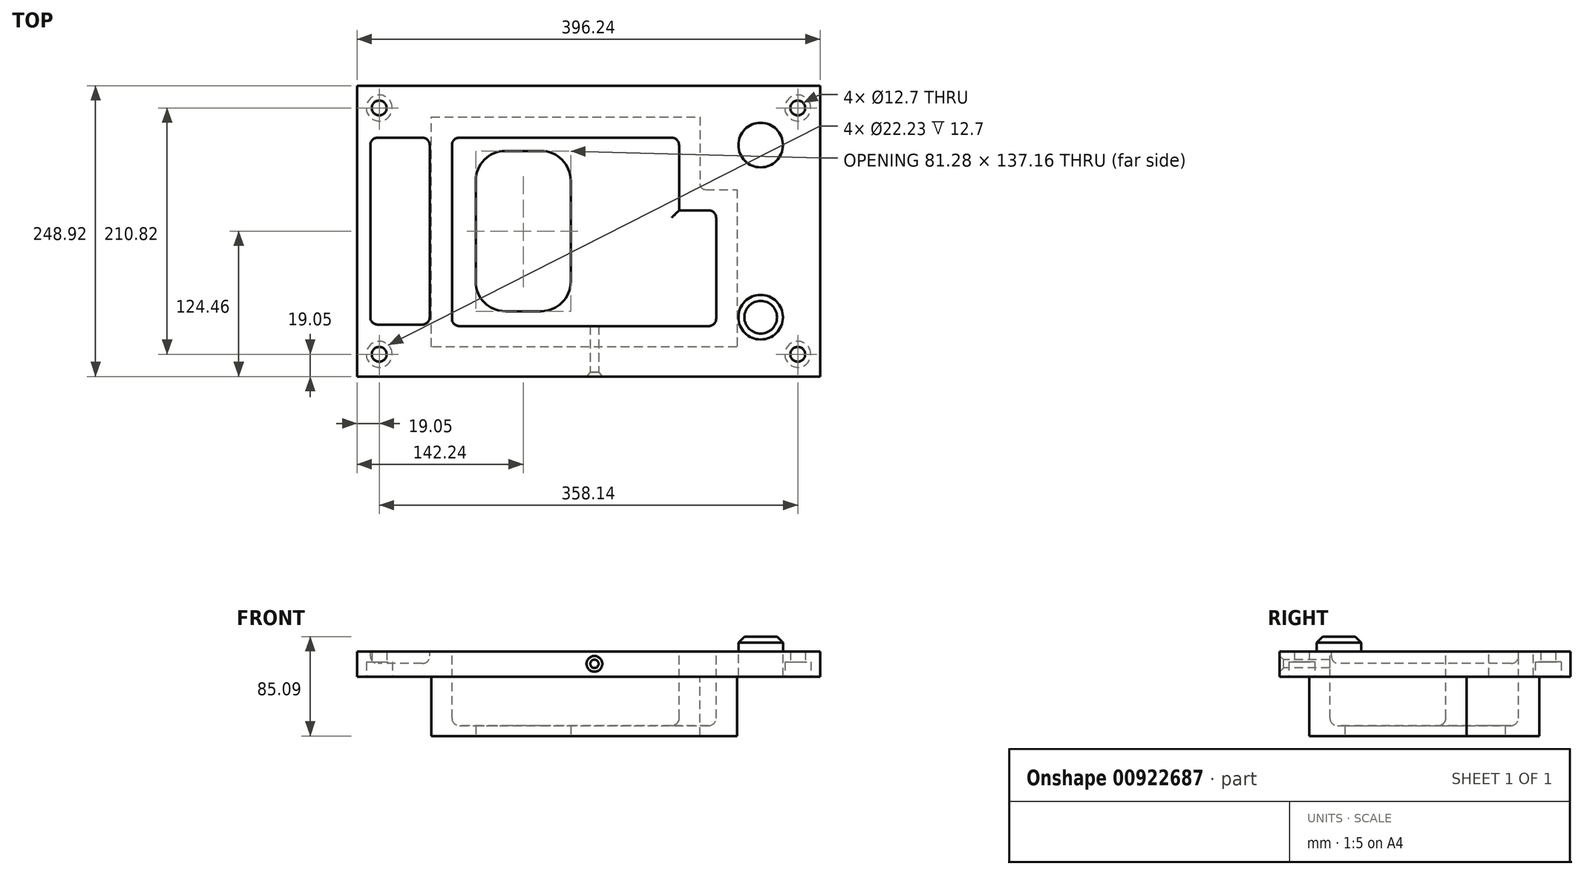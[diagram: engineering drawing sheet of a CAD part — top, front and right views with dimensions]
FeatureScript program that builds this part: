
annotation { "Feature Type Name" : "Feature", "Feature Type Description" : "" }
export const myFeature = defineFeature(function(context is Context, id is Id, definition is map)
    precondition{}
    {
        {
            var Q0;
            Q0=qCreatedBy(makeId("Top.planeOp"),FACE);
            var sketch = newSketch(context, id + "F0", { "sketchPlane" : qUnion([Q0])});
            skLineSegment(sketch, "E0.bottom", {"start": v(198.12, 124.46) * mm, "end": v(-198.12, 124.46) * mm});
            skLineSegment(sketch, "E0.top", {"start": v(198.12, -124.46) * mm, "end": v(-198.12, -124.46) * mm});
            skLineSegment(sketch, "E0.left", {"start": v(198.12, 124.46) * mm, "end": v(198.12, -124.46) * mm});
            skLineSegment(sketch, "E0.right", {"start": v(-198.12, 124.46) * mm, "end": v(-198.12, -124.46) * mm});
            skPoint(sketch, "E0.middle", {"position": v(0, 0) * mm});
            skSolve(sketch);
        }
        {
            var Q0;
            Q0 = qSketchRegion(id + "F0", true);
            extrude(context, id + "F1", {"entities" : qUnion([Q0]), "oppositeDirection" : true, "depth" : 21.59 * mm, "offsetDistance" : 25.4 * mm});
        }
        {
            var Q0;
            Q0=makeQuery(id+"F1.opExtrude","CAP_FACE",FACE,{"disambiguationData":[OSD([sQuery(id+"F0.wireOp",EDGE,"E0.bottom"),sQuery(id+"F0.wireOp",EDGE,"E0.top"),sQuery(id+"F0.wireOp",EDGE,"E0.left"),sQuery(id+"F0.wireOp",EDGE,"E0.right")])],"isStart":false});
            var sketch = newSketch(context, id + "F2", { "sketchPlane" : qUnion([Q0])});
            skLineSegment(sketch, "E1", {"start": v(-134.62, 99.06) * mm, "end": v(-134.62, -97.79) * mm});
            skLineSegment(sketch, "E2", {"start": v(-134.62, -97.79) * mm, "end": v(95.25, -97.79) * mm});
            skLineSegment(sketch, "E3", {"start": v(95.25, -97.8) * mm, "end": v(95.25, -35.56) * mm});
            skLineSegment(sketch, "E4", {"start": v(95.25, -35.56) * mm, "end": v(127, -35.56) * mm});
            skLineSegment(sketch, "E5", {"start": v(127, -35.56) * mm, "end": v(127, 99.06) * mm});
            skLineSegment(sketch, "E6", {"start": v(127, 99.06) * mm, "end": v(-134.62, 99.06) * mm});
            skSolve(sketch);
        }
        {
            var Q0;
            Q0 = qSketchRegion(id + "F2", true);
            extrude(context, id + "F3", {"entities" : qUnion([Q0]), "operationType" : NewBodyOperationType.ADD, "depth" : 50.8 * mm, "offsetDistance" : 25.4 * mm});
        }
        {
            var Q0;
            Q0=makeQuery(id+"F1.opExtrude","CAP_FACE",FACE,{"disambiguationData":[OSD([sQuery(id+"F0.wireOp",EDGE,"E0.bottom"),sQuery(id+"F0.wireOp",EDGE,"E0.top"),sQuery(id+"F0.wireOp",EDGE,"E0.left"),sQuery(id+"F0.wireOp",EDGE,"E0.right")])],"isStart":true});
            var sketch = newSketch(context, id + "F4", { "sketchPlane" : qUnion([Q0])});
            skLineSegment(sketch, "E7.0", {"start": v(127, -99.06) * mm, "end": v(-134.62, -99.06) * mm, "construction": true});
            skLineSegment(sketch, "E8.0", {"start": v(127, 35.56) * mm, "end": v(127, -99.06) * mm, "construction": true});
            skPoint(sketch, "E9.0", {"position": v(111.12, 35.56) * mm});
            skLineSegment(sketch, "E10.0", {"start": v(95.25, 97.8) * mm, "end": v(95.25, 35.56) * mm, "construction": true});
            skLineSegment(sketch, "E11.0", {"start": v(95.25, 35.56) * mm, "end": v(127, 35.56) * mm, "construction": true});
            skLineSegment(sketch, "E12.0", {"start": v(-134.62, 97.79) * mm, "end": v(95.25, 97.79) * mm, "construction": true});
            skLineSegment(sketch, "E13.0", {"start": v(-134.62, -99.06) * mm, "end": v(-134.62, 97.79) * mm, "construction": true});
            skLineSegment(sketch, "E14", {"start": v(109.22, -81.28) * mm, "end": v(109.22, 17.78) * mm});
            skLineSegment(sketch, "E15", {"start": v(109.22, 17.78) * mm, "end": v(77.47, 17.78) * mm});
            skLineSegment(sketch, "E16", {"start": v(77.47, 17.78) * mm, "end": v(77.47, 80) * mm});
            skLineSegment(sketch, "E17", {"start": v(77.47, 80) * mm, "end": v(-116.84, 80) * mm});
            skLineSegment(sketch, "E18", {"start": v(-116.84, 80) * mm, "end": v(-116.84, -81.28) * mm});
            skLineSegment(sketch, "E19", {"start": v(-116.84, -81.28) * mm, "end": v(109.22, -81.28) * mm});
            skSolve(sketch);
        }
        {
            var Q0;
            Q0 = qSketchRegion(id + "F4", true);
            extrude(context, id + "F5", {"entities" : qUnion([Q0]), "operationType" : NewBodyOperationType.REMOVE, "oppositeDirection" : true, "depth" : 63.5 * mm, "offsetDistance" : 25.4 * mm});
        }
        {
            var Q0;
            Q0=makeQuery(id+"F5.boolean.opBoolean","COPY",FACE,{"derivedFrom":makeQuery(id+"F5.opExtrude","CAP_FACE",FACE,{"disambiguationData":[OSD([sQuery(id+"F4.wireOp",EDGE,"E14"),sQuery(id+"F4.wireOp",EDGE,"E15"),sQuery(id+"F4.wireOp",EDGE,"E16"),sQuery(id+"F4.wireOp",EDGE,"E17"),sQuery(id+"F4.wireOp",EDGE,"E18"),sQuery(id+"F4.wireOp",EDGE,"E19")])],"isStart":false})});
            var Q1;
            Q1=makeQuery(id+"F5.boolean.opBoolean","COPY",EDGE,{"derivedFrom":makeQuery(id+"F5.opExtrude","SWEPT_EDGE",EDGE,{"disambiguationData":[OSD([sQuery(id+"F4.wireOp",EDGE,"E14"),sQuery(id+"F4.wireOp",EDGE,"E19")])]})});
            var Q2;
            Q2=makeQuery(id+"F5.boolean.opBoolean","COPY",EDGE,{"derivedFrom":makeQuery(id+"F5.opExtrude","SWEPT_EDGE",EDGE,{"disambiguationData":[OSD([sQuery(id+"F4.wireOp",EDGE,"E18"),sQuery(id+"F4.wireOp",EDGE,"E19")])]})});
            var Q3;
            Q3=makeQuery(id+"F5.boolean.opBoolean","COPY",EDGE,{"derivedFrom":makeQuery(id+"F5.opExtrude","SWEPT_EDGE",EDGE,{"disambiguationData":[OSD([sQuery(id+"F4.wireOp",EDGE,"E17"),sQuery(id+"F4.wireOp",EDGE,"E18")])]})});
            var Q4;
            Q4=makeQuery(id+"F5.boolean.opBoolean","COPY",EDGE,{"derivedFrom":makeQuery(id+"F5.opExtrude","SWEPT_EDGE",EDGE,{"disambiguationData":[OSD([sQuery(id+"F4.wireOp",EDGE,"E14"),sQuery(id+"F4.wireOp",EDGE,"E15")])]})});
            var Q5;
            Q5=makeQuery(id+"F5.boolean.opBoolean","COPY",EDGE,{"derivedFrom":makeQuery(id+"F5.opExtrude","SWEPT_EDGE",EDGE,{"disambiguationData":[OSD([sQuery(id+"F4.wireOp",EDGE,"E16"),sQuery(id+"F4.wireOp",EDGE,"E17")])]})});
            fillet(context, id + "F6", {"entities" : qUnion([Q0, Q1, Q2, Q3, Q4, Q5]), "radius" : 6.35 * mm, "tangentPropagation" : true, "allowEdgeOverflow" : false});
        }
        {
            var Q0;
            Q0=makeQuery(id+"F3.opExtrude","SWEPT_EDGE",EDGE,{"disambiguationData":[OSD([sQuery(id+"F2.wireOp",EDGE,"E3"),sQuery(id+"F2.wireOp",EDGE,"E4")])]});
            fillet(context, id + "F7", {"entities" : qUnion([Q0]), "radius" : 5.08 * mm, "tangentPropagation" : true, "allowEdgeOverflow" : false});
        }
        {
            var Q0;
            Q0=makeQuery(id+"F3.opExtrude","CAP_FACE",FACE,{"disambiguationData":[OSD([sQuery(id+"F2.wireOp",EDGE,"E1"),sQuery(id+"F2.wireOp",EDGE,"E2"),sQuery(id+"F2.wireOp",EDGE,"E3"),sQuery(id+"F2.wireOp",EDGE,"E4"),sQuery(id+"F2.wireOp",EDGE,"E5"),sQuery(id+"F2.wireOp",EDGE,"E6")])],"isStart":false});
            var sketch = newSketch(context, id + "F8", { "sketchPlane" : qUnion([Q0])});
            skLineSegment(sketch, "E20.bottom", {"start": v(-96.52, -68.58) * mm, "end": v(-15.24, -68.58) * mm});
            skLineSegment(sketch, "E20.top", {"start": v(-96.52, 68.58) * mm, "end": v(-15.24, 68.58) * mm});
            skLineSegment(sketch, "E20.left", {"start": v(-96.52, -68.58) * mm, "end": v(-96.52, 68.58) * mm});
            skLineSegment(sketch, "E20.right", {"start": v(-15.24, -68.58) * mm, "end": v(-15.24, 68.58) * mm});
            skPoint(sketch, "E20.middle", {"position": v(-55.88, 0) * mm});
            skSolve(sketch);
        }
        {
            var Q0;
            Q0 = qSketchRegion(id + "F8", true);
            extrude(context, id + "F9", {"entities" : qUnion([Q0]), "operationType" : NewBodyOperationType.REMOVE, "endBound" : BoundingType.THROUGH_ALL, "oppositeDirection" : true, "depth" : 25.4 * mm, "offsetDistance" : 25.4 * mm});
        }
        {
            var Q0;
            Q0=makeQuery(id+"F1.opExtrude","CAP_FACE",FACE,{"disambiguationData":[OSD([sQuery(id+"F0.wireOp",EDGE,"E0.bottom"),sQuery(id+"F0.wireOp",EDGE,"E0.top"),sQuery(id+"F0.wireOp",EDGE,"E0.left"),sQuery(id+"F0.wireOp",EDGE,"E0.right")])],"isStart":true});
            var sketch = newSketch(context, id + "F10", { "sketchPlane" : qUnion([Q0])});
            skLineSegment(sketch, "E21.bottom", {"start": v(-135.9, 80) * mm, "end": v(-186.7, 80) * mm});
            skLineSegment(sketch, "E21.top", {"start": v(-135.9, -80) * mm, "end": v(-186.7, -80) * mm});
            skLineSegment(sketch, "E21.left", {"start": v(-135.9, 80) * mm, "end": v(-135.9, -80) * mm});
            skLineSegment(sketch, "E21.right", {"start": v(-186.7, 80) * mm, "end": v(-186.7, -80) * mm});
            skPoint(sketch, "E21.middle", {"position": v(-161.3, 0) * mm});
            skSolve(sketch);
        }
        {
            var Q0;
            Q0 = qSketchRegion(id + "F10", true);
            extrude(context, id + "F11", {"entities" : qUnion([Q0]), "operationType" : NewBodyOperationType.REMOVE, "oppositeDirection" : true, "depth" : 10.4 * mm, "offsetDistance" : 25.4 * mm});
        }
        {
            var Q0;
            Q0=makeQuery(id+"F11.boolean.opBoolean","COPY",FACE,{"derivedFrom":makeQuery(id+"F11.opExtrude","CAP_FACE",FACE,{"disambiguationData":[OSD([sQuery(id+"F10.wireOp",EDGE,"E21.bottom"),sQuery(id+"F10.wireOp",EDGE,"E21.top"),sQuery(id+"F10.wireOp",EDGE,"E21.left"),sQuery(id+"F10.wireOp",EDGE,"E21.right")])],"isStart":false})});
            var Q1;
            Q1=makeQuery(id+"F11.boolean.opBoolean","COPY",EDGE,{"derivedFrom":makeQuery(id+"F11.opExtrude","SWEPT_EDGE",EDGE,{"disambiguationData":[OSD([sQuery(id+"F10.wireOp",EDGE,"E21.bottom"),sQuery(id+"F10.wireOp",EDGE,"E21.right")])]})});
            var Q2;
            Q2=makeQuery(id+"F11.boolean.opBoolean","COPY",EDGE,{"derivedFrom":makeQuery(id+"F11.opExtrude","SWEPT_EDGE",EDGE,{"disambiguationData":[OSD([sQuery(id+"F10.wireOp",EDGE,"E21.bottom"),sQuery(id+"F10.wireOp",EDGE,"E21.left")])]})});
            var Q3;
            Q3=makeQuery(id+"F11.boolean.opBoolean","COPY",EDGE,{"derivedFrom":makeQuery(id+"F11.opExtrude","SWEPT_EDGE",EDGE,{"disambiguationData":[OSD([sQuery(id+"F10.wireOp",EDGE,"E21.top"),sQuery(id+"F10.wireOp",EDGE,"E21.left")])]})});
            var Q4;
            Q4=makeQuery(id+"F11.boolean.opBoolean","COPY",EDGE,{"derivedFrom":makeQuery(id+"F11.opExtrude","SWEPT_EDGE",EDGE,{"disambiguationData":[OSD([sQuery(id+"F10.wireOp",EDGE,"E21.top"),sQuery(id+"F10.wireOp",EDGE,"E21.right")])]})});
            fillet(context, id + "F12", {"entities" : qUnion([Q0, Q1, Q2, Q3, Q4]), "radius" : 6.35 * mm, "tangentPropagation" : true, "allowEdgeOverflow" : false});
        }
        {
            var Q0;
            Q0=makeQuery(id+"F1.opExtrude","CAP_FACE",FACE,{"disambiguationData":[OSD([sQuery(id+"F0.wireOp",EDGE,"E0.bottom"),sQuery(id+"F0.wireOp",EDGE,"E0.top"),sQuery(id+"F0.wireOp",EDGE,"E0.left"),sQuery(id+"F0.wireOp",EDGE,"E0.right")])],"isStart":true});
            var sketch = newSketch(context, id + "F13", { "sketchPlane" : qUnion([Q0])});
            skLineSegment(sketch, "E22.bottom", {"start": v(160.02, 86.36) * mm, "end": v(134.62, 86.36) * mm});
            skLineSegment(sketch, "E22.top", {"start": v(160.02, 60.96) * mm, "end": v(134.62, 60.96) * mm});
            skLineSegment(sketch, "E22.left", {"start": v(160.02, 86.36) * mm, "end": v(160.02, 60.96) * mm});
            skLineSegment(sketch, "E22.right", {"start": v(134.62, 86.36) * mm, "end": v(134.62, 60.96) * mm});
            skPoint(sketch, "E22.middle", {"position": v(147.32, 73.66) * mm});
            skCircle(sketch, "E23", {"center": v(147.32, -73.66) * mm, "radius": 19.05 * mm});
            skSolve(sketch);
        }
        {
            var Q0;
            Q0=makeQuery(id+"F13.imprint","IMPRINT",FACE,{"disambiguationData":[TD([[makeQuery(id+"F13.imprint","IMPRINT",EDGE,{"derivedFrom":sQuery(id+"F13.wireOp",EDGE,"E23")}),1.0]])]});
            extrude(context, id + "F14", {"entities" : qUnion([Q0]), "operationType" : NewBodyOperationType.ADD, "depth" : 12.7 * mm, "offsetDistance" : 25.4 * mm});
        }
        {
            var Q0;
            Q0=makeQuery(id+"F14.opExtrude","CAP_FACE",FACE,{"disambiguationData":[OSD([sQuery(id+"F13.wireOp",EDGE,"E22.bottom"),sQuery(id+"F13.wireOp",EDGE,"E22.top"),sQuery(id+"F13.wireOp",EDGE,"E22.left"),sQuery(id+"F13.wireOp",EDGE,"E22.right")])],"isStart":false});
            var Q1;
            Q1=makeQuery(id+"F14.opExtrude","CAP_FACE",FACE,{"disambiguationData":[OSD([sQuery(id+"F13.wireOp",EDGE,"E23")])],"isStart":false});
            chamfer(context, id + "F15", {"entities" : qUnion([Q0, Q1]), "width" : 5.08 * mm, "tangentPropagation" : true});
        }
        {
            var Q0;
            Q0=makeQuery(id+"F1.opExtrude","SWEPT_FACE",FACE,{"disambiguationData":[OSD([sQuery(id+"F0.wireOp",EDGE,"E0.top")])]});
            var sketch = newSketch(context, id + "F16", { "sketchPlane" : qUnion([Q0])});
            skPoint(sketch, "E24", {"position": v(5.08, -10.67) * mm});
            skSolve(sketch);
        }
        {
            var Q0;
            Q0=sQuery(id+"F16.wireOp",VERTEX,"E24");
            var Q1;
            Q1=makeQuery(id+"F1.opExtrude","SWEPT_BODY",BODY,{"disambiguationData":[OSD([sQuery(id+"F0.wireOp",EDGE,"E0.bottom"),sQuery(id+"F0.wireOp",EDGE,"E0.top"),sQuery(id+"F0.wireOp",EDGE,"E0.left"),sQuery(id+"F0.wireOp",EDGE,"E0.right")])]});
            hole(context, id + "F17", {"style" : HoleStyle.C_SINK, "endStyle" : HoleEndStyle.BLIND, "standardTappedOrClearance" : lookupTablePath({ "fit" : "Normal (ASME)", "standard" : "ANSI", "size" : "1/4", "type" : "Clearance" }), "standardBlindInLast" : lookupTablePath({ "fit" : "Normal", "standard" : "ANSI", "size" : "1/4", "type" : "Clearance" }), "holeDiameter" : 7.14 * mm, "cSinkDiameter" : 13.5 * mm, "cSinkAngle" : 82 * degree, "majorDiameter" : 6.35 * mm, "holeDepth" : 127 * mm, "isTappedThrough" : true, "tappedDepth" : 12.7 * mm, "tapClearance" : 3, "locations" : qUnion([Q0]), "scope" : qUnion([Q1])});
        }
        {
            var Q0;
            Q0=makeQuery(id+"F2.imprint","IMPRINT",FACE,{"disambiguationData":[TD([[makeQuery(id+"F2.imprint","IMPRINT",EDGE,{"derivedFrom":sQuery(id+"F2.wireOp",EDGE,"E1")}),-1.0]])]});
            var sketch = newSketch(context, id + "F18", { "sketchPlane" : qUnion([Q0])});
            skLineSegment(sketch, "E25.bottom", {"start": v(179.07, -105.41) * mm, "end": v(-179.07, -105.41) * mm});
            skLineSegment(sketch, "E25.top", {"start": v(179.07, 105.41) * mm, "end": v(-179.07, 105.41) * mm});
            skLineSegment(sketch, "E25.left", {"start": v(179.07, -105.41) * mm, "end": v(179.07, 105.41) * mm});
            skLineSegment(sketch, "E25.right", {"start": v(-179.07, -105.41) * mm, "end": v(-179.07, 105.41) * mm});
            skPoint(sketch, "E25.middle", {"position": v(0, 0) * mm});
            skSolve(sketch);
        }
        {
            var Q0;
            Q0=sQuery(id+"F18.wireOp",VERTEX,"E25.top.end");
            var Q1;
            Q1=sQuery(id+"F18.wireOp",VERTEX,"E25.top.start");
            var Q2;
            Q2=sQuery(id+"F18.wireOp",VERTEX,"E25.bottom.start");
            var Q3;
            Q3=sQuery(id+"F18.wireOp",VERTEX,"E25.bottom.end");
            var Q4;
            Q4=makeQuery(id+"F1.opExtrude","SWEPT_BODY",BODY,{"disambiguationData":[OSD([sQuery(id+"F0.wireOp",EDGE,"E0.bottom"),sQuery(id+"F0.wireOp",EDGE,"E0.top"),sQuery(id+"F0.wireOp",EDGE,"E0.left"),sQuery(id+"F0.wireOp",EDGE,"E0.right")])]});
            hole(context, id + "F19", {"style" : HoleStyle.C_BORE, "endStyle" : HoleEndStyle.THROUGH, "holeDiameter" : 12.7 * mm, "cBoreDiameter" : 22.22 * mm, "cBoreDepth" : 12.7 * mm, "majorDiameter" : 6.35 * mm, "isTappedThrough" : true, "tappedDepth" : 12.7 * mm, "tapClearance" : 3, "locations" : qUnion([Q0, Q1, Q2, Q3]), "scope" : qUnion([Q4])});
        }
        {
            var Q0;
            Q0=makeQuery(id+"F1.opExtrude","CAP_FACE",FACE,{"disambiguationData":[OSD([sQuery(id+"F0.wireOp",EDGE,"E0.bottom"),sQuery(id+"F0.wireOp",EDGE,"E0.top"),sQuery(id+"F0.wireOp",EDGE,"E0.left"),sQuery(id+"F0.wireOp",EDGE,"E0.right")])],"isStart":true});
            var sketch = newSketch(context, id + "F20", { "sketchPlane" : qUnion([Q0])});
            skCircle(sketch, "E26", {"center": v(147.32, 73.66) * mm, "radius": 19.05 * mm});
            skSolve(sketch);
        }
        {
            var Q0;
            Q0 = qSketchRegion(id + "F20", true);
            extrude(context, id + "F21", {"entities" : qUnion([Q0]), "operationType" : NewBodyOperationType.REMOVE, "endBound" : BoundingType.THROUGH_ALL, "oppositeDirection" : true, "depth" : 25.4 * mm, "offsetDistance" : 25.4 * mm});
        }
        {
            var Q0;
            Q0=makeQuery(id+"F9.boolean.opBoolean","COPY",EDGE,{"derivedFrom":makeQuery(id+"F9.opExtrude","SWEPT_EDGE",EDGE,{"disambiguationData":[OSD([sQuery(id+"F8.wireOp",EDGE,"E20.top"),sQuery(id+"F8.wireOp",EDGE,"E20.right")])]})});
            var Q1;
            Q1=makeQuery(id+"F9.boolean.opBoolean","COPY",EDGE,{"derivedFrom":makeQuery(id+"F9.opExtrude","SWEPT_EDGE",EDGE,{"disambiguationData":[OSD([sQuery(id+"F8.wireOp",EDGE,"E20.bottom"),sQuery(id+"F8.wireOp",EDGE,"E20.right")])]})});
            var Q2;
            Q2=makeQuery(id+"F9.boolean.opBoolean","COPY",EDGE,{"derivedFrom":makeQuery(id+"F9.opExtrude","SWEPT_EDGE",EDGE,{"disambiguationData":[OSD([sQuery(id+"F8.wireOp",EDGE,"E20.bottom"),sQuery(id+"F8.wireOp",EDGE,"E20.left")])]})});
            var Q3;
            Q3=makeQuery(id+"F9.boolean.opBoolean","COPY",EDGE,{"derivedFrom":makeQuery(id+"F9.opExtrude","SWEPT_EDGE",EDGE,{"disambiguationData":[OSD([sQuery(id+"F8.wireOp",EDGE,"E20.top"),sQuery(id+"F8.wireOp",EDGE,"E20.left")])]})});
            fillet(context, id + "F22", {"entities" : qUnion([Q0, Q1, Q2, Q3]), "radius" : 25.4 * mm, "tangentPropagation" : true, "allowEdgeOverflow" : false});
        }
    });
